# Revit family: Haworth_Circa_Light
name_source: partatom
category: Lighting Fixtures
revit_build: Autodesk Revit 2018 (Build: 20170223_1515(x64)
units: mm (PartAtom-declared; Revit-internal decimal feet)

## family parameters
Always vertical = Yes
Cut with Voids When Loaded = No
Light Source = Yes
OmniClass Number = 23.80.70.11.14
OmniClass Title = General Luminaries, Directional
Part Type = Normal
Room Calculation Point = No
Round Connector Dimension = Use Diameter
Shared = No
Work Plane-Based = No

## types (4) — shared parameters
Assembly Code = D5020200
Color Filter = 16777215
Dimming Lamp Color Temperature Shift = <None>
Emit Shape Visible in Rendering = No
Emit from Circle Diameter = 12"
Manufacturer = Haworth
Pedestal Finish = Haworth _ Metal _ Stainless Steel
Photometric Web File = generic
Revision Number = 1
Size = Verify Final Dim. w/ Haworth
URL = http://www.haworth.com
URL - Product = https://www.haworth.com
Warranty = http://www.haworth.com
Wattage Comments = 9-11W 120V 60Hz

## per-type parameters (varying)
| type | Actual Depth | Actual Height | Actual Width | Base | Base Radius | Base Thickness Offset | Description | Desk Lamp | Floor Lamp | Grommet Mount | Height | Lamp Radius | Model | Pedestal Control | Tilt Angle | Top Rod Length | with Pedestal |
| LRF1-5208 - Floor Light with Pedestal | 16" | 52" | 16" | Yes | 7" | 25/64" | Haworth Circa Floor Light with Pedestal | No | Yes | No | 52 in. | 8" | LRF1-5208 | Yes | 90.00° | 23 3/4" | Yes |
| LRT1-1408 - Grommet Mounted Light | 12" | 14" | 12" | No | 5" | 0" | Haworth Circa Grommet Mounted Light | No | No | Yes | 14 in. | 6" | LRT1-1408-G | No | 60.00° | 14" | No |
| LRT1-1408 - Table Light | 12" | 14" | 12" | Yes | 5" | 0" | Haworth Circa Table Light | Yes | No | No | 14 in. | 6" | LRT1-1408 | No | 60.00° | 14" | No |
| LRF0-5208 - Floor Light without Pedestal | 16" | 52" | 16" | Yes | 7" | 25/64" | Haworth Circa Floor Light without Pedestal | No | Yes | No | 52 in. | 8" | LRF0-5208 | No | 60.00° | 23 3/4" | No |

## geometry (parser evidence)
native form markers: Sweep x3
no freeform markers — native parametric forms only
